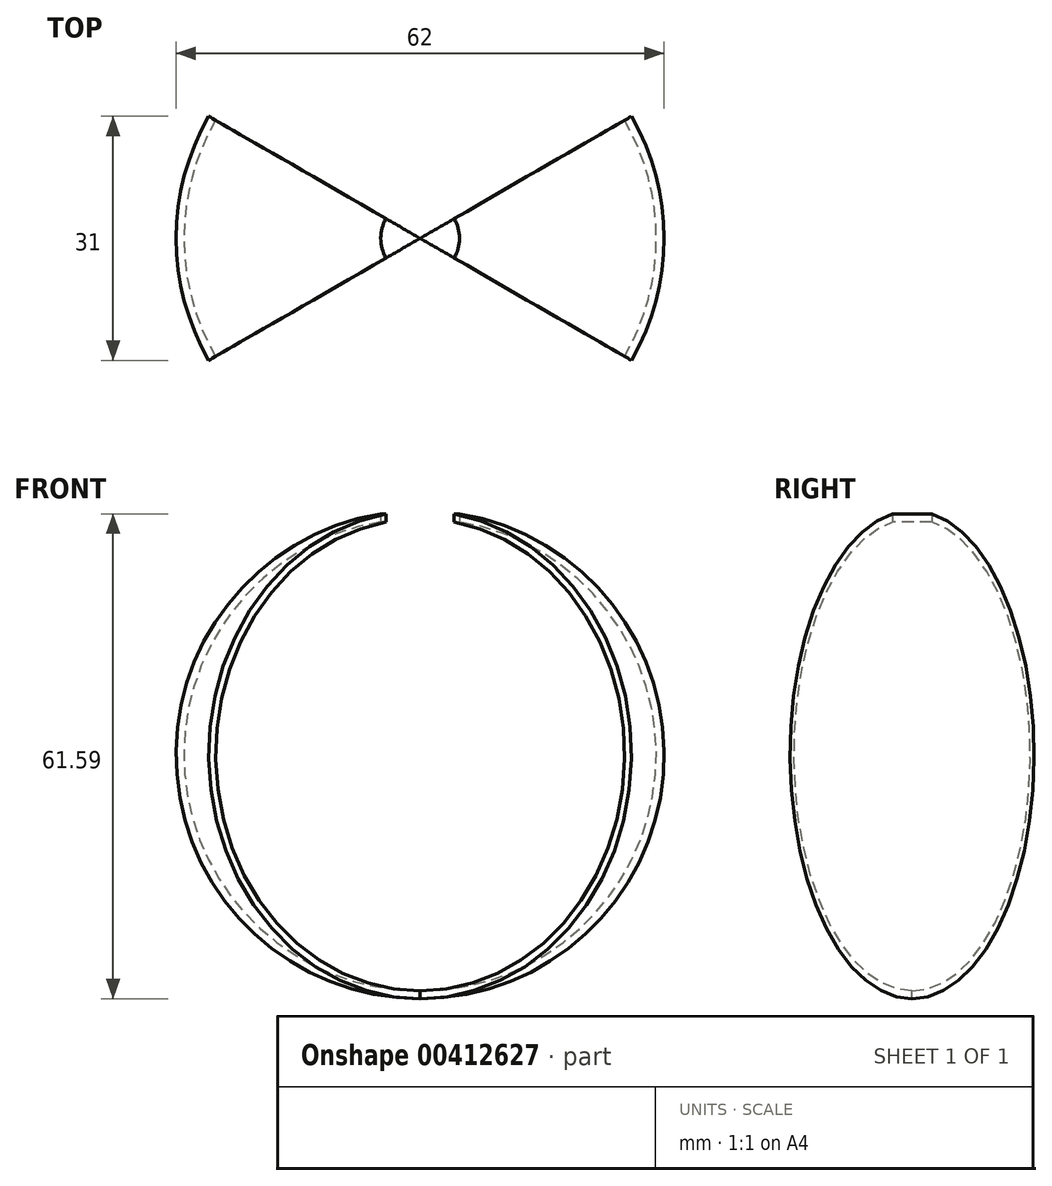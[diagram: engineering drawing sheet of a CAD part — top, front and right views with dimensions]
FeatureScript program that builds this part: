
annotation { "Feature Type Name" : "Feature", "Feature Type Description" : "" }
export const myFeature = defineFeature(function(context is Context, id is Id, definition is map)
    precondition{}
    {
        {
            var Q0;
            Q0=qCreatedBy(makeId("Front.planeOp"),FACE);
            var sketch = newSketch(context, id + "F0", { "sketchPlane" : qUnion([Q0])});
            skLineSegment(sketch, "E0", {"start": v(0, 31) * mm, "end": v(0, 30) * mm});
            skArc(sketch, "E1", {"start": v(0, 30) * mm, "mid": v(21.21, 21.21) * mm, "end": v(30, 0) * mm});
            skArc(sketch, "E2", {"start": v(0, 31) * mm, "mid": v(21.92, 21.92) * mm, "end": v(31, 0) * mm});
            skArc(sketch, "E3.MirrorCS", {"start": v(0, -31) * mm, "mid": v(21.92, -21.92) * mm, "end": v(31, 0) * mm});
            skArc(sketch, "E4.MirrorCS", {"start": v(0, -30) * mm, "mid": v(21.21, -21.21) * mm, "end": v(30, 0) * mm});
            skLineSegment(sketch, "E5.MirrorCS", {"start": v(0, -31) * mm, "end": v(0, -30) * mm});
            skSolve(sketch);
        }
        {
            var Q0;
            Q0=makeQuery(id+"F0.imprint","IMPRINT",FACE,{"disambiguationData":[TD([[makeQuery(id+"F0.imprint","IMPRINT",EDGE,{"derivedFrom":sQuery(id+"F0.wireOp",EDGE,"E0")}),1.0]])]});
            var Q1;
            Q1=sQuery(id+"F0.wireOp",EDGE,"E0");
            revolve(context, id + "F1", {"entities" : qUnion([Q0]), "axis" : qUnion([Q1]), "revolveType" : RevolveType.TWO_DIRECTIONS, "angle" : 30 * degree, "angleBack" : 330 * degree});
        }
        {
            var Q0;
            Q0=qCreatedBy(makeId("Top.planeOp"),FACE);
            var sketch = newSketch(context, id + "F2", { "sketchPlane" : qUnion([Q0])});
            skCircle(sketch, "E6", {"center": v(0, 0) * mm, "radius": 5 * mm});
            skSolve(sketch);
        }
        {
            var Q0;
            Q0 = qSketchRegion(id + "F2", true);
            extrude(context, id + "F3", {"entities" : qUnion([Q0]), "operationType" : NewBodyOperationType.REMOVE, "depth" : 33 * mm});
        }
        {
            var Q0;
            Q0=makeQuery(id+"F1.opRevolve","SWEPT_BODY",BODY,{"disambiguationData":[OSD([sQuery(id+"F0.wireOp",EDGE,"E0"),sQuery(id+"F0.wireOp",EDGE,"E1"),sQuery(id+"F0.wireOp",EDGE,"E2"),sQuery(id+"F0.wireOp",EDGE,"E3.MirrorCS"),sQuery(id+"F0.wireOp",EDGE,"57hetBob-tCqX-0m47-gQhI-LsQ76PUadTMj")])]});
            var Q1;
            Q1=qCreatedBy(makeId("Right.planeOp"),FACE);
            mirror(context, id + "F4", {"entities" : qUnion([Q0]), "mirrorPlane" : qUnion([Q1])});
        }
    });
